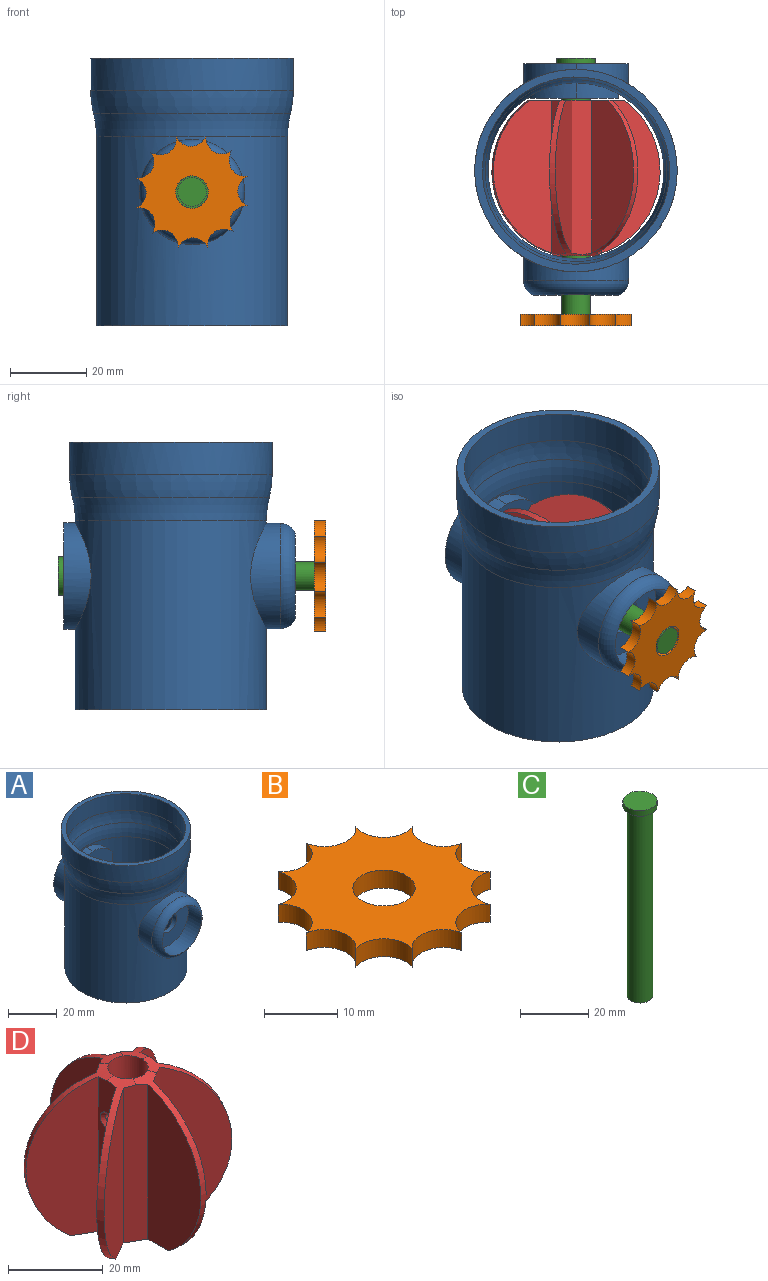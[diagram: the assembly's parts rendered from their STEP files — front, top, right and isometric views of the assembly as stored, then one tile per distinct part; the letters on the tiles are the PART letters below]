
ASSEMBLY  parts=4 mates=3
PART A: 26 faces, bbox 69.8x69.8x70 mm
  f0: cylinder r=25mm len=50mm, axis (0,0,1), area 6524.3mm2, adj f3,f6,f12,f22,f23
  f1: cylinder r=23mm len=49.47mm, axis (0,0,1), area 6490.8mm2, adj f2,f3,f9,f15,f16,f17,f18,f19
  f2: cylinder r=4.5mm len=9mm, axis (0,-1,0), area 62.8mm2, adj f1,f14
  f3: plane 50x50mm, normal (0,0,-1), area 301.6mm2, adj f0,f1
  f4: cylinder r=26.5mm len=53mm, axis (0,0,1), area 1394.3mm2, adj f5,f7
  f5: plane 53x53mm, normal (0,0,1), area 320.4mm2, adj f4,f8
  f6: torus R=50mm, axis (0,0,1), area 974mm2, adj f0,f7
  f7: torus R=1.5mm, axis (0,0,-1), area 1012.5mm2, adj f4,f6
  f8: cylinder r=24.5mm len=49mm, axis (0,0,1), area 1289.1mm2, adj f5,f10
  f9: torus R=50mm, axis (0,0,1), area 969.4mm2, adj f1,f10
  f10: torus R=1.5mm, axis (0,0,-1), area 861.3mm2, adj f8,f9
  f11: cylinder r=11.25mm len=22.5mm, axis (0,1,0), area 530.1mm2, adj f13,f14
  f12: cylinder r=13.75mm len=27.5mm, axis (0,1,0), area 501.4mm2, adj f0,f13
  f13: torus R=9.75mm, axis (0,-1,0), area 383.9mm2, adj f11,f12
  f14: plane 22.5x22.5mm, normal (0,-1,0), area 334mm2, adj f2,f11
  f15: cylinder r=14mm len=11.25mm, axis (0,1,0), area 38.5mm2, adj f1,f16,f19,f20
  f16: cylinder r=14mm len=12.96mm, axis (0,-1,0), area 40.4mm2, adj f1,f15,f20
  f17: cylinder r=14mm len=11.25mm, axis (0,1,0), area 38.5mm2, adj f1,f18,f19,f20
  f18: cylinder r=14mm len=12.96mm, axis (0,-1,0), area 40.4mm2, adj f1,f17,f20
  f19: plane 15.97x1.06mm, normal (1,0,0), area 16.9mm2, adj f1,f15,f17,f20
  f20: plane 28x24.21mm, normal (0,-1,0), area 503.5mm2, adj f1,f15,f16,f17,f18,f19,f25
  f21: plane 28x27.5mm, normal (0,1,0), area 204.1mm2, adj f22,f23,f24
  f22: cylinder r=14mm len=28mm, axis (0,-1,0), area 218.2mm2, adj f0,f21,f23
  f23: cylinder r=14mm len=28mm, axis (0,1,0), area 218.1mm2, adj f0,f21,f22
  f24: cylinder r=11.25mm len=22.5mm, axis (0,1,0), area 353.4mm2, adj f21,f25
  f25: cone r=0mm half-angle=59deg, axis (0,1,0), area 386.5mm2, adj f20,f24
PART B: 15 faces, bbox 30x30x3 mm
  f0: cylinder r=4.27mm len=5.76mm, axis (0,0,-1), area 29.2mm2, adj f1,f11,f13,f14
  f1: cylinder r=4.27mm len=7.5mm, axis (0,0,-1), area 29.2mm2, adj f0,f2,f13,f14
  f2: cylinder r=4.27mm len=7.5mm, axis (0,0,-1), area 29.2mm2, adj f1,f3,f13,f14
  f3: cylinder r=4.27mm len=5.76mm, axis (0,0,-1), area 29.2mm2, adj f2,f4,f13,f14
  f4: cylinder r=4.27mm len=7.5mm, axis (0,0,-1), area 29.2mm2, adj f3,f5,f13,f14
  f5: cylinder r=4.27mm len=7.5mm, axis (0,0,-1), area 29.2mm2, adj f4,f6,f13,f14
  f6: cylinder r=4.27mm len=5.76mm, axis (0,0,-1), area 29.2mm2, adj f5,f7,f13,f14
  f7: cylinder r=4.27mm len=7.5mm, axis (0,0,-1), area 29.2mm2, adj f6,f8,f13,f14
  f8: cylinder r=4.27mm len=7.5mm, axis (0,0,-1), area 29.2mm2, adj f7,f9,f13,f14
  f9: cylinder r=4.25mm len=5.77mm, axis (0,0,-1), area 29.3mm2, adj f8,f10,f13,f14
  f10: cylinder r=4.27mm len=7.5mm, axis (0,0,-1), area 29.2mm2, adj f9,f11,f13,f14
  f11: cylinder r=4.27mm len=7.5mm, axis (0,0,-1), area 29.2mm2, adj f0,f10,f13,f14
  f12: cylinder r=4.25mm len=8.5mm, axis (0,0,-1), area 80.1mm2, adj f13,f14
  f13: plane 30x30mm, normal (0,0,1), area 451.4mm2, adj f0,f1,f2,f3,f4,f5,f6,f7
  f14: plane 30x30mm, normal (0,0,-1), area 451.4mm2, adj f0,f1,f2,f3,f4,f5,f6,f7
PART C: 5 faces, bbox 10x10x70 mm
  f0: cylinder r=3.75mm len=68mm, axis (0,0,-1), area 1602.2mm2, adj f1,f3
  f1: plane 7.5x7.5mm, normal (0,0,-1), area 44.2mm2, adj f0
  f2: cylinder r=5mm len=10mm, axis (0,0,1), area 62.8mm2, adj f3,f4
  f3: plane 10x10mm, normal (0,0,-1), area 34.4mm2, adj f0,f2
  f4: plane 10x10mm, normal (0,0,1), area 78.5mm2, adj f2
PART D: 30 faces, bbox 42.1x45x40.7 mm
  f0: cylinder r=4.25mm len=40.7mm, axis (0,0,-1), area 1075.8mm2, adj f19,f20,f21,f22,f23,f24,f25,f26
  f1: plane 39.96x15.75mm, normal (-1,0,0), area 485.8mm2, adj f2,f24,f25
  f2: plane 40.35x4.66mm, normal (-0.5,0.87,0), area 215.6mm2, adj f1,f3,f23,f24,f25
  f3: plane 39.96x13.64mm, normal (0.5,0.87,0), area 485.8mm2, adj f2,f23,f25
  f4: plane 39.96x13.64mm, normal (-0.5,-0.87,0), area 485.8mm2, adj f5,f23,f25
  f5: plane 40.35x5.38mm, normal (-1,0,0), area 203.1mm2, adj f4,f6,f21,f23,f25,f27
  f6: plane 39.96x13.64mm, normal (-0.5,0.87,0), area 485.8mm2, adj f5,f21,f25
  f7: plane 39.96x13.64mm, normal (0.5,-0.87,0), area 485.8mm2, adj f8,f21,f25
  f8: plane 40.35x4.66mm, normal (-0.5,-0.87,0), area 215.6mm2, adj f7,f9,f19,f21,f25
  f9: plane 39.96x15.75mm, normal (-1,0,0), area 485.8mm2, adj f8,f19,f25
  f10: plane 39.96x15.75mm, normal (1,0,0), area 485.8mm2, adj f11,f19,f25
  f11: plane 40.35x4.66mm, normal (0.5,-0.87,0), area 215.6mm2, adj f10,f12,f19,f20,f25
  f12: plane 39.96x13.64mm, normal (-0.5,-0.87,0), area 485.8mm2, adj f11,f20,f25
  f13: plane 39.96x13.64mm, normal (0.5,0.87,0), area 485.8mm2, adj f14,f20,f25
  f14: plane 40.35x5.38mm, normal (1,0,0), area 203.1mm2, adj f13,f15,f20,f22,f25,f29
  f15: plane 39.96x13.64mm, normal (0.5,-0.87,0), area 485.8mm2, adj f14,f22,f25
  f16: plane 39.96x13.64mm, normal (-0.5,0.87,0), area 485.8mm2, adj f17,f22,f25
  f17: plane 40.35x4.66mm, normal (0.5,0.87,0), area 215.6mm2, adj f16,f18,f22,f24,f25
  f18: plane 39.96x15.75mm, normal (1,0,0), area 485.8mm2, adj f17,f24,f25
  f19: cylinder r=22.5mm len=40.7mm, axis (-1,0,0), area 93.4mm2, adj f0,f8,f9,f10,f11,f20,f21,f25
  f20: cylinder r=22.5mm len=40.7mm, axis (-0.5,-0.87,0), area 93.4mm2, adj f0,f11,f12,f13,f14,f19,f22,f25
  f21: cylinder r=22.5mm len=40.7mm, axis (-0.5,0.87,0), area 93.4mm2, adj f0,f5,f6,f7,f8,f19,f23,f25
  f22: cylinder r=22.5mm len=40.7mm, axis (0.5,-0.87,0), area 93.4mm2, adj f0,f14,f15,f16,f17,f20,f24,f25
  f23: cylinder r=22.5mm len=40.7mm, axis (0.5,0.87,0), area 93.4mm2, adj f0,f2,f3,f4,f5,f21,f24,f25
  f24: cylinder r=22.5mm len=40.7mm, axis (1,0,0), area 93.4mm2, adj f0,f1,f2,f17,f18,f22,f23,f25
  f25: plane 25.61x22.98mm, normal (0,0,-1), area 134.4mm2, adj f0,f1,f2,f3,f4,f5,f6,f7
  f26: cylinder r=1.2mm len=2.4mm, axis (-1,0,0), area 9.7mm2, adj f0,f27
  f27: cone r=1.2mm half-angle=45deg, axis (-1,0,0), area 11.4mm2, adj f5,f26
  f28: cylinder r=1.2mm len=2.4mm, axis (1,0,0), area 9.7mm2, adj f0,f29
  f29: cone r=1.2mm half-angle=45deg, axis (1,0,0), area 11.4mm2, adj f14,f28
PLACE A t=(34.21,13.39,-9.54)mm fixed
PLACE B rot(axis=(0.28,-0.68,0.68),149.2deg) t=(34.21,-24.15,25.46)mm
PLACE C rot(axis=(-0.28,-0.68,-0.68),149.2deg) t=(34.21,-27.15,25.46)mm
PLACE D rot(axis=(0.87,0.35,-0.35),98.1deg) t=(34.21,35.79,25.46)mm
MATE fastened C.f0 <-> D.f0  axis (0,-1,0) through (34.21,-27.15,25.46)mm
MATE revolute D.f0 <-> A.f2  axis (0,1,0) through (34.21,-9.15,25.46)mm
MATE fastened B.f12 <-> C.f0  axis (0,-1,0) through (34.21,-27.15,25.46)mm
